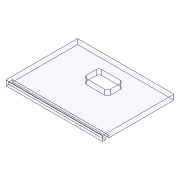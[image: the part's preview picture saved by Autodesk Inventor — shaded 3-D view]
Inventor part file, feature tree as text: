
AUTODESK INVENTOR PART (.ipt)
format: ipt  version: 2018.3 (Build 223284000, 284)  size: 115,712 bytes
history: native  units: in
note: dims shown in document units (in); Inventor stores cm internally (conversion verified against a paired STEP export)
features: extrude x3, sketch x3, fillet x1
ambient origin geometry x8: Origin, YZ Plane, XZ Plane, XY Plane, X Axis, Y Axis, Z Axis, Center Point
bodies: Solid1 (feature_tree)
feature tree (7):
  extrude  "Extrusion1"  Depth=2.19in
  extrude  "Extrusion2"  Depth=0.35in
  fillet  "Fillet1"  Radius=0.118in
  extrude  "Extrusion6"  Depth=0.55in
  sketch  "Sketch1"  dims[d0=1.625in d1=2.19in]
  sketch  "Sketch2"  dims[d2=0.118in d3=0.0in d7=0.35in d9=0.118in d10=0.0in]
  sketch  "Sketch6"  dims[d11=0.0625in d17=0.55in d22=0.275in d23=0.175in d24=1.095in d25=1.095in d26=1.1125in d31=0.0625in d32=0.085in d33=0.049in d34=0.0in]
